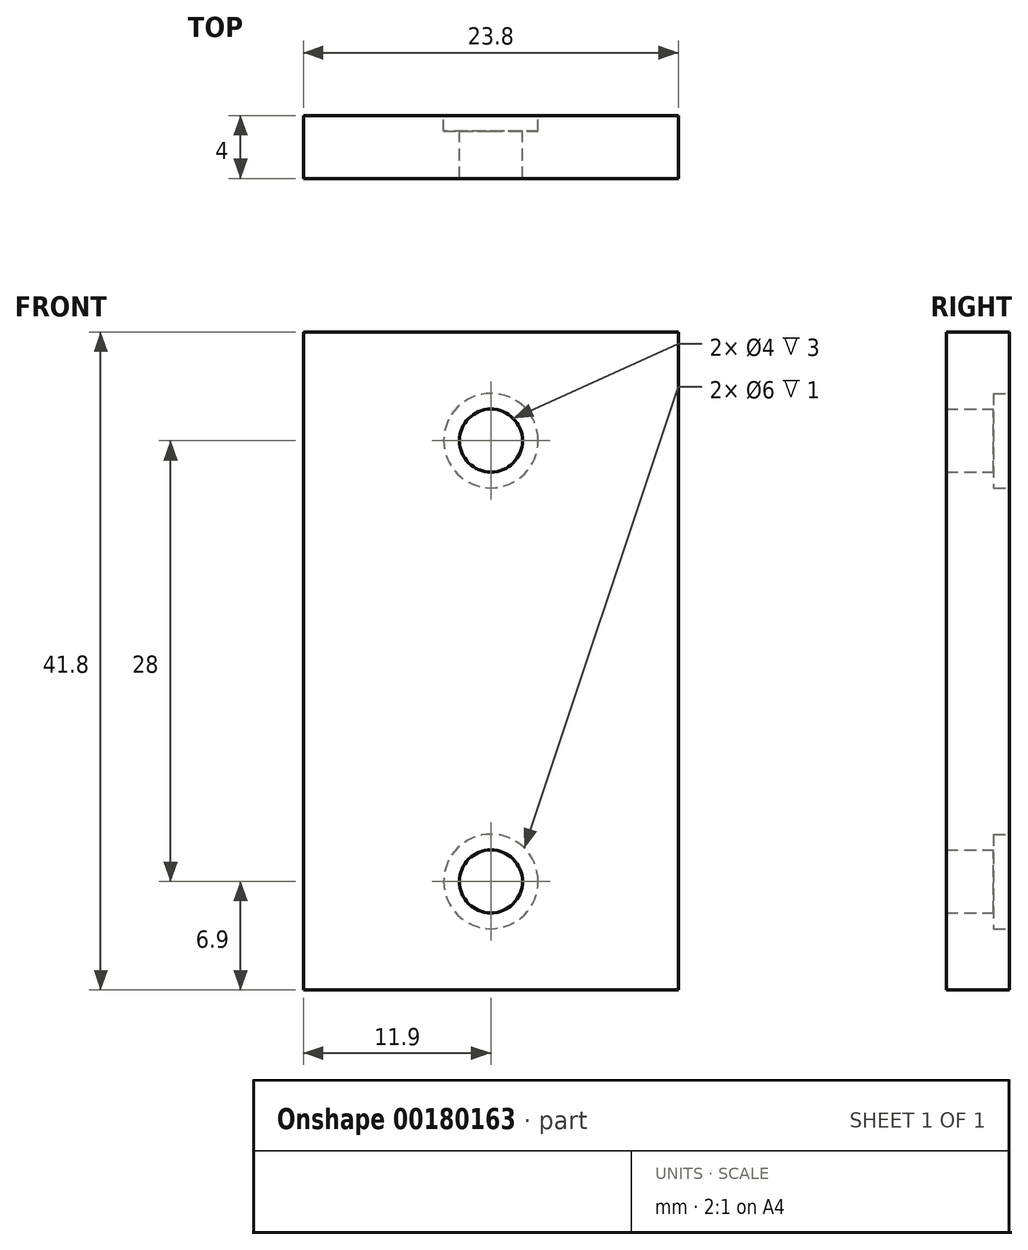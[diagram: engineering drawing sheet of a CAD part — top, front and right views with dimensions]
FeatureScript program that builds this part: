
annotation { "Feature Type Name" : "Feature", "Feature Type Description" : "" }
export const myFeature = defineFeature(function(context is Context, id is Id, definition is map)
    precondition{}
    {
        {
            var Q0;
            Q0=qCreatedBy(makeId("Front.planeOp"),FACE);
            var sketch = newSketch(context, id + "F0", { "sketchPlane" : qUnion([Q0])});
            skLineSegment(sketch, "E0.bottom", {"start": v(11.9, 20.9) * mm, "end": v(-11.9, 20.9) * mm});
            skLineSegment(sketch, "E0.top", {"start": v(11.9, -20.9) * mm, "end": v(-11.9, -20.9) * mm});
            skLineSegment(sketch, "E0.left", {"start": v(11.9, 20.9) * mm, "end": v(11.9, -20.9) * mm});
            skLineSegment(sketch, "E0.right", {"start": v(-11.9, 20.9) * mm, "end": v(-11.9, -20.9) * mm});
            skPoint(sketch, "E0.middle", {"position": v(0, 0) * mm});
            skLineSegment(sketch, "E1", {"start": v(0, 0) * mm, "end": v(0, 14) * mm});
            skLineSegment(sketch, "E2", {"start": v(0, 0) * mm, "end": v(0, -14) * mm});
            skLineSegment(sketch, "E3", {"start": v(0, 14) * mm, "end": v(0, -14) * mm});
            skCircle(sketch, "E4", {"center": v(0, 14) * mm, "radius": 2 * mm});
            skCircle(sketch, "E5", {"center": v(0, -14) * mm, "radius": 2 * mm});
            skLineSegment(sketch, "E6", {"start": v(0, 20.9) * mm, "end": v(0, 14) * mm});
            skLineSegment(sketch, "E7", {"start": v(0, -20.9) * mm, "end": v(0, -14) * mm});
            skSolve(sketch);
        }
        {
            var Q0;
            Q0=makeQuery(id+"F0.imprint","IMPRINT",FACE,{"disambiguationData":[TD([[makeQuery(id+"F0.imprint","IMPRINT",EDGE,{"derivedFrom":sQuery(id+"F0.wireOp",EDGE,"E0.bottom")}),1.0]])]});
            extrude(context, id + "F1", {"entities" : qUnion([Q0]), "depth" : 4 * mm});
        }
        {
            var Q0;
            Q0=makeQuery(id+"F1.opExtrude","CAP_FACE",FACE,{"disambiguationData":[OSD([sQuery(id+"F0.wireOp",EDGE,"E0.bottom"),sQuery(id+"F0.wireOp",EDGE,"E0.top"),sQuery(id+"F0.wireOp",EDGE,"E0.left"),sQuery(id+"F0.wireOp",EDGE,"E0.right"),sQuery(id+"F0.wireOp",EDGE,"E4"),sQuery(id+"F0.wireOp",EDGE,"E5")])],"isStart":true});
            var sketch = newSketch(context, id + "F2", { "sketchPlane" : qUnion([Q0])});
            skCircle(sketch, "E8", {"center": v(0, 14) * mm, "radius": 3 * mm});
            skCircle(sketch, "E9", {"center": v(0, -14) * mm, "radius": 3 * mm});
            skSolve(sketch);
        }
        {
            var Q0;
            Q0=makeQuery(id+"F2.imprint","IMPRINT",FACE,{"disambiguationData":[TD([[makeQuery(id+"F2.imprint","IMPRINT",EDGE,{"derivedFrom":sQuery(id+"F2.wireOp",EDGE,"E8")}),1.0]])]});
            var Q1;
            Q1=makeQuery(id+"F2.imprint","IMPRINT",FACE,{"disambiguationData":[TD([[makeQuery(id+"F2.imprint","IMPRINT",EDGE,{"derivedFrom":sQuery(id+"F2.wireOp",EDGE,"E9")}),1.0]])]});
            extrude(context, id + "F3", {"entities" : qUnion([Q0, Q1]), "operationType" : NewBodyOperationType.REMOVE, "oppositeDirection" : true, "depth" : 1 * mm});
        }
    });
